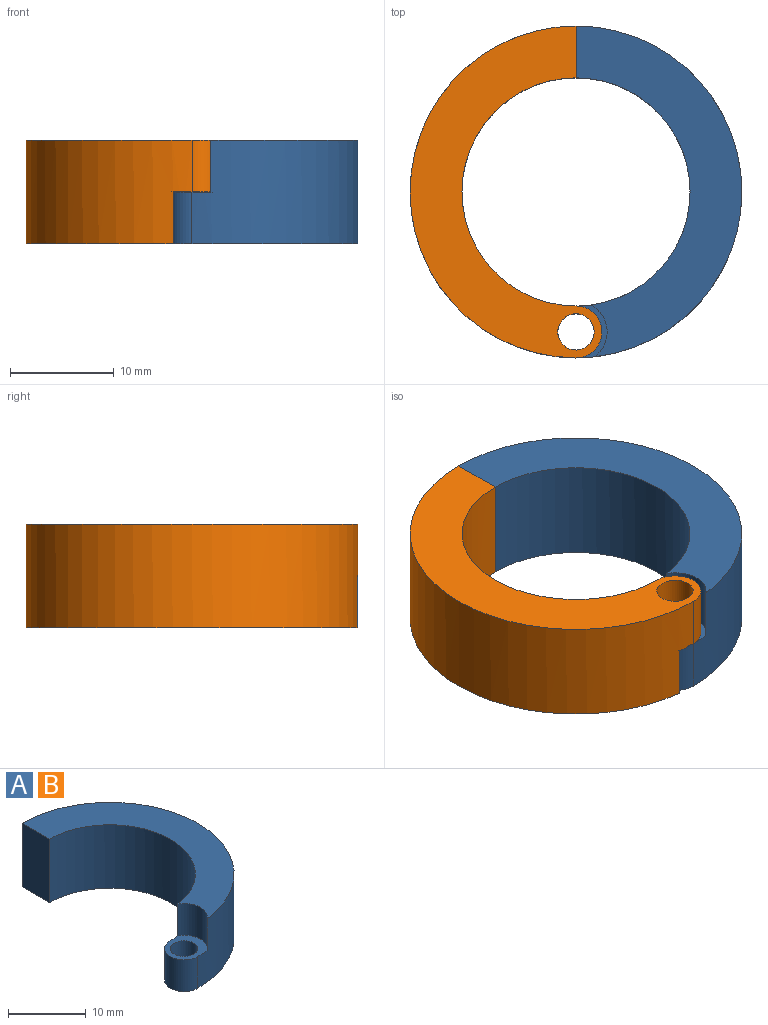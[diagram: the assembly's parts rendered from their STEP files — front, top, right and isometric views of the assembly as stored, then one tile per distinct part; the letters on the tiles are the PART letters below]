
ASSEMBLY  parts=2 mates=1
PART A: 9 faces, bbox 18.5x32x10 mm
  f0: plane 5.5x5.1mm, normal (0,0,1), area 13.2mm2, adj f1,f2,f3,f5,f7
  f1: cylinder r=11mm len=22mm, axis (0,0,-1), area 338.1mm2, adj f0,f2,f4,f6,f7,f8
  f2: cylinder r=2.5mm len=5mm, axis (0,0,-1), area 39.3mm2, adj f0,f1,f3,f6
  f3: cylinder r=16mm len=32mm, axis (0,0,-1), area 493.6mm2, adj f0,f2,f4,f6,f7,f8
  f4: plane 10x5mm, normal (-1,0,0), area 50mm2, adj f1,f3,f6,f8
  f5: cylinder r=1.75mm len=5mm, axis (0,0,-1), area 55mm2, adj f0,f6
  f6: plane 32x18.5mm, normal (0,0,-1), area 212.3mm2, adj f1,f2,f3,f4,f5
  f7: cylinder r=3mm len=5mm, axis (0,0,-1), area 29.6mm2, adj f0,f1,f3,f8
  f8: plane 31.9x16mm, normal (0,0,1), area 199mm2, adj f1,f3,f4,f7
PART B: same geometry as A
PLACE A t=(-28.58,-2.17,10.65)mm
PLACE B rot(axis=(0,1,0),180deg) t=(-28.58,-2.17,20.65)mm
MATE parallel B.f4 <-> A.f4  axis (1,0,0) through (-28.58,11.33,15.65)mm
